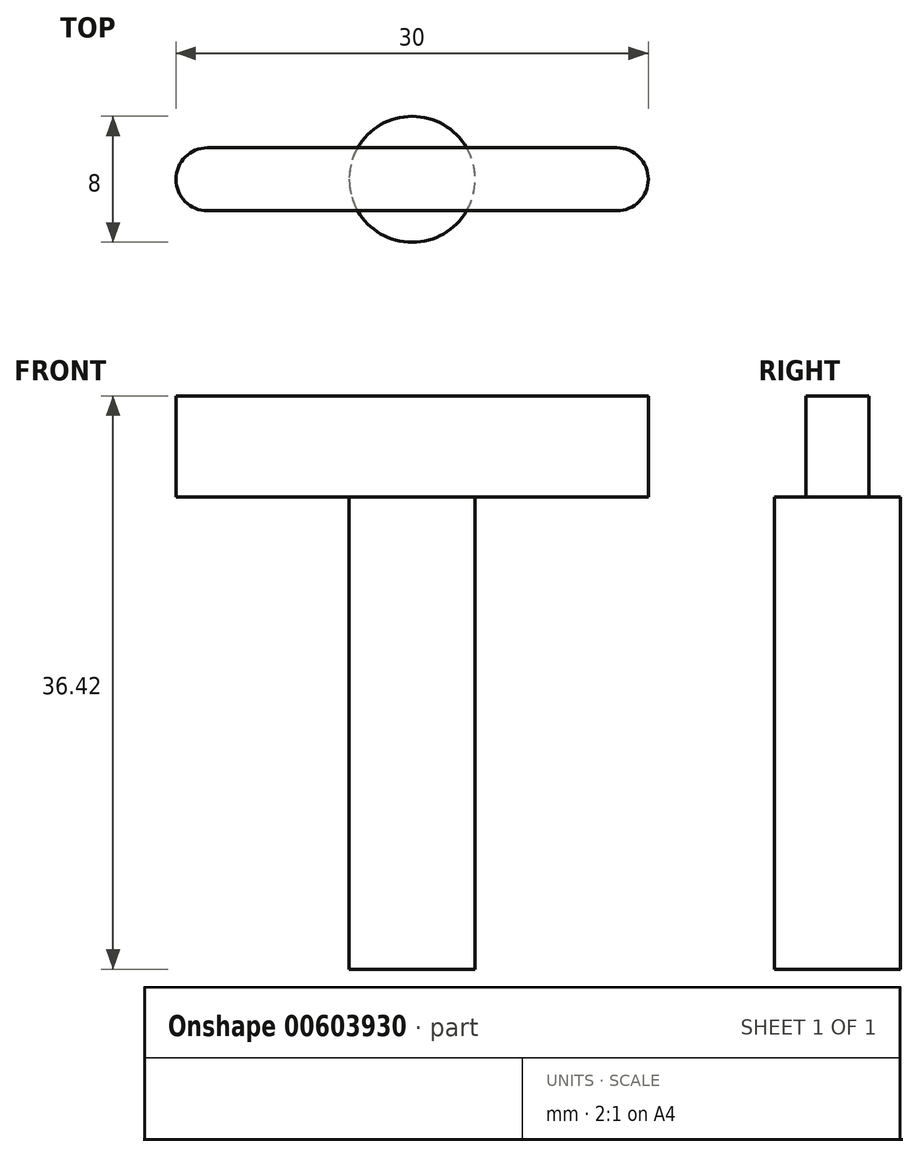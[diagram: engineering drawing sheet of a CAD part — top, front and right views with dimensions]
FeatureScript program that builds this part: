
annotation { "Feature Type Name" : "Feature", "Feature Type Description" : "" }
export const myFeature = defineFeature(function(context is Context, id is Id, definition is map)
    precondition{}
    {
        {
            var Q0;
            Q0=qCreatedBy(makeId("Top.planeOp"),FACE);
            var sketch = newSketch(context, id + "F0", { "sketchPlane" : qUnion([Q0])});
            skArc(sketch, "E0", {"start": v(-13, 2) * mm, "mid": v(-15, 0) * mm, "end": v(-13, -2) * mm});
            skLineSegment(sketch, "E1", {"start": v(-13, 2) * mm, "end": v(13, 2) * mm});
            skLineSegment(sketch, "E2", {"start": v(-13, -2) * mm, "end": v(13, -2) * mm});
            skArc(sketch, "E3", {"start": v(13, -2) * mm, "mid": v(15, 0) * mm, "end": v(13, 2) * mm});
            skPoint(sketch, "E3.centerSnap0", {"position": v(-11.8, 0) * mm});
            skLineSegment(sketch, "E4", {"start": v(-13, 0) * mm, "end": v(-15, 0) * mm, "construction": true});
            skLineSegment(sketch, "E5", {"start": v(0, 0) * mm, "end": v(15, 0) * mm, "construction": true});
            skSolve(sketch);
        }
        {
            var Q0;
            Q0=qSketchRegion(id+"F0",true);
            extrude(context, id + "F1", {"entities" : qUnion([Q0]), "depth" : 6.42 * mm, "offsetDistance" : 25 * mm});
        }
        {
            var Q0;
            Q0=makeQuery(id+"F1.opExtrude","CAP_FACE",FACE,{"disambiguationData":[OSD([sQuery(id+"F0.wireOp",EDGE,"E0"),sQuery(id+"F0.wireOp",EDGE,"E1"),sQuery(id+"F0.wireOp",EDGE,"E2"),sQuery(id+"F0.wireOp",EDGE,"E3")])],"isStart":true});
            var sketch = newSketch(context, id + "F2", { "sketchPlane" : qUnion([Q0])});
            skCircle(sketch, "E6", {"center": v(0, 0) * mm, "radius": 4 * mm});
            skSolve(sketch);
        }
        {
            var Q0;
            Q0=qSketchRegion(id+"F2",true);
            extrude(context, id + "F3", {"entities" : qUnion([Q0]), "operationType" : NewBodyOperationType.ADD, "depth" : 30 * mm, "offsetDistance" : 25 * mm});
        }
    });
